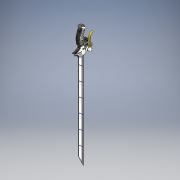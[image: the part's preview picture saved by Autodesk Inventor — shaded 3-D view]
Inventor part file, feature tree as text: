
AUTODESK INVENTOR PART (.ipt)
format: ipt  version: 2021 (Build 250183000, 183)  size: 3,606,528 bytes
history: native  units: in
note: dims shown in document units (in); Inventor stores cm internally (conversion verified against a paired STEP export)
features: sketch x34, extrude x32, chamfer x8, plane x8, mirror x4, fillet x2, emboss x2, sweep x1, projected_geometry x1
ambient origin geometry x8: Origin, YZ Plane, XZ Plane, XY Plane, X Axis, Y Axis, Z Axis, Center Point
bodies: Solid1 (feature_tree)
feature tree (92):
  extrude  "Extrusion1"  Depth=0.035in TaperAngle=0.0deg
  extrude  "Extrusion2"  Depth=0.05in TaperAngle=45.0deg
  chamfer  "Chamfer1"  Distance=0.025in
  chamfer  "Chamfer2"  Distance=0.225in
  extrude  "Extrusion3"  Depth=0.025in TaperAngle=45.0deg
  extrude  "Extrusion4"  Depth=0.01in TaperAngle=0.0deg
  chamfer  "Chamfer3"  Distance=0.02in
  chamfer  "Chamfer4"  Distance=0.185in
  extrude  "Extrusion5"  Depth=0.05in TaperAngle=0.0deg
  plane  "Work Plane1"
  mirror  "Mirror1"
  extrude  "Extrusion6"  Depth=0.25in TaperAngle=0.0deg
  extrude  "Extrusion7"  Depth=7.0in TaperAngle=0.0deg
  extrude  "Extrusion8"  Depth=0.14in
  plane  "Work Plane2"
  extrude  "Extrusion9"  Depth=0.3in TaperAngle=0.0deg
  extrude  "Extrusion10"  Depth=0.11in TaperAngle=0.0deg
  extrude  "Extrusion11"  Depth=0.125in TaperAngle=0.0deg
  extrude  "Extrusion13"  Depth=0.15in TaperAngle=0.0deg
  extrude  "Extrusion14"  Depth=0.15in TaperAngle=0.0deg
  extrude  "Extrusion15"  Depth=0.125in
  chamfer  "Chamfer5"  Distance=0.0005in
  chamfer  "Chamfer6"  Distance=0.0005in
  sketch  "Sketch16"  dims[d60=0.25in d61=0.0in d62=0.11in d63=0.0in]
  extrude  "Extrusion16"  Depth=0.02in TaperAngle=0.0deg
  extrude  "Extrusion17"  Depth=0.01in TaperAngle=0.0deg
  extrude  "Extrusion18"  Depth=0.01in TaperAngle=0.0deg
  chamfer  "Chamfer11"  Distance=0.0025in
  extrude  "Extrusion19"  Depth=0.01in TaperAngle=45.0deg
  extrude  "Extrusion20"  Depth=0.005in TaperAngle=0.0deg
  extrude  "Extrusion21"  Depth=0.1in TaperAngle=0.0deg
  sketch  "Sketch23"  dims[d88=0.05in d89=0.0in d90=0.125in]
  sketch  "3D Sketch2"
  sketch  "Sketch24"  dims[d107=2.3622in d109=1.0in d110=0.3937in d112=1.0in d114=0.0005in d115=0.0in]
  sketch  "Sketch25"  dims[d116=2.3622in d118=1.0in d119=0.3937in d121=1.0in d123=0.0005in d124=0.0in]
  sketch  "Sketch26"  dims[d125=0.05in d126=0.02in d127=0.0in]
  sketch  "Sketch27"  dims[d128=0.02in d129=0.0in d130=0.01in d131=0.0in]
  sweep  "Sweep1"
  extrude  "Extrusion22"  [1 undecoded]
  extrude  "Extrusion23"  [1 undecoded]
  fillet  "Fillet1"  [1 undecoded]
  extrude  "Extrusion25"  [1 undecoded]
  extrude  "Extrusion26"  [1 undecoded]
  plane  "Work Plane3"
  mirror  "Mirror3"
  fillet  "Fillet2"  [1 undecoded]
  extrude  "Extrusion27"  [1 undecoded]
  extrude  "Extrusion28"  [1 undecoded]
  plane  "Work Plane4"
  mirror  "Mirror4"
  extrude  "Extrusion29"  [1 undecoded]
  extrude  "Extrusion30"  [1 undecoded]
  extrude  "Extrusion31"  [1 undecoded]
  plane  "Work Plane5"
  emboss  "Emboss1"
  emboss  "Emboss2"
  chamfer  "Chamfer12"  [1 undecoded]
  extrude  "Extrusion32"  [1 undecoded]
  plane  "Work Plane6"
  mirror  "Mirror5"
  plane  "Work Plane8"
  extrude  "Extrusion33"  [1 undecoded]
  extrude  "Extrusion34"  [1 undecoded]
  sketch  "Sketch1"  dims[d0=0.2in d1=0.0in d2=0.035in d3=0.23in d4=0.0in d5=0.0in]
  sketch  "Sketch2"  dims[d6=0.035in d7=0.125in d8=45.0deg d9=0.05in d10=0.125in d11=45.0deg d12=0.025in d13=0.0in d14=0.225in d15=0.0in]
  sketch  "Sketch3"  dims[d16=0.025in d17=0.225in d18=0.0in d19=0.0in d20=0.025in d21=0.125in d22=45.0deg]
  sketch  "Sketch4"  dims[d23=0.025in d24=0.125in d25=45.0deg d26=0.01in d27=0.0in d28=0.02in d29=0.0in d30=0.185in d31=0.0in]
  sketch  "Sketch5"  dims[d32=0.02in d33=0.22in d34=0.0in d35=0.0in d36=0.05in d37=0.0in]
  sketch  "Sketch6"  dims[d38=0.015in d39=0.215in d40=0.0in d41=0.0in d42=0.25in d43=0.0in]
  sketch  "Sketch7"  dims[d46=0.125in d47=0.0in d48=7.0in d49=0.0in]
  sketch  "Sketch13"  dims[d50=1.0in d51=0.0in d52=0.14in d53=0.125in d54=0.0687in]
  sketch  "Sketch15"  dims[d55=0.14in d56=0.125in d57=0.0687in d58=0.3in d59=0.0in]
  sketch  "Sketch20"  dims[d76=0.075in d77=0.125in d78=45.0deg d79=0.125in d80=0.0in]
  sketch  "Sketch21"  dims[d81=0.325in d82=0.0in d83=0.15in d84=0.0in]
  sketch  "Sketch22"  dims[d85=0.0in d86=0.15in d87=0.0in]
  projected_geometry  "Projected Loop1"
  sketch  "Sketch28"  dims[d132=0.005in d133=0.0in d134=0.01in d135=0.0in d136=0.0025in d137=0.0in]
  sketch  "Sketch29"  dims[d138=0.0025in d139=0.0in d140=0.01in d141=0.125in d142=45.0deg]
  sketch  "Sketch30"  dims[d143=0.0in d144=0.005in d145=0.0in]
  sketch  "Sketch32"  dims[d146=0.075in d147=0.0in d148=0.1in d149=0.0in]
  sketch  "Sketch33"
  sketch  "Sketch34"
  sketch  "Sketch35"
  sketch  "Sketch36"
  sketch  "Sketch37"
  sketch  "Sketch38"
  sketch  "Sketch39"
  sketch  "Sketch40"
  sketch  "Sketch41"
  plane  "Work Plane7"
  sketch  "Sketch42"
  sketch  "Sketch43"
note: 15 required parameter values undecoded (feature->parameter linkage not recoverable at this tier; creation-order binding heuristic only, values carry confidence <= 0.55)
